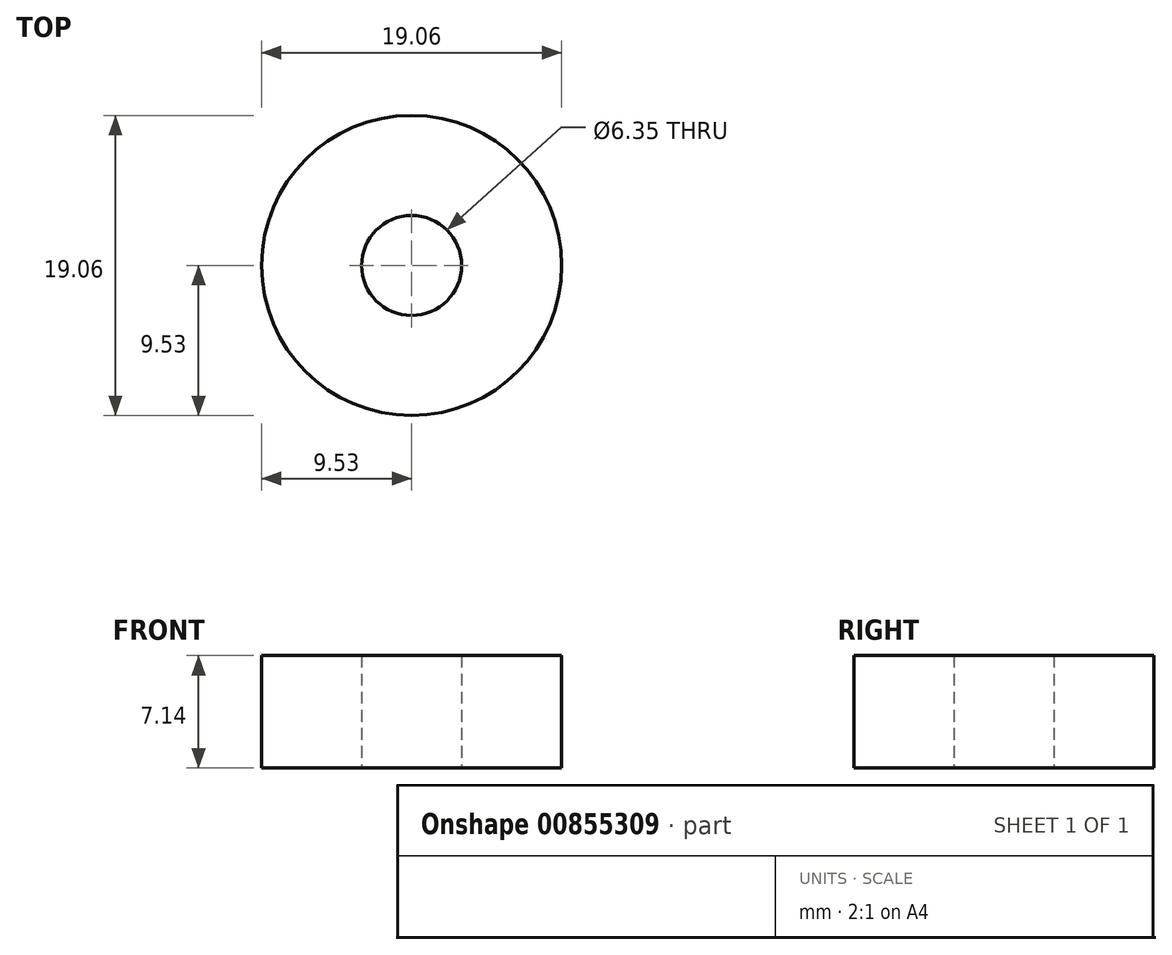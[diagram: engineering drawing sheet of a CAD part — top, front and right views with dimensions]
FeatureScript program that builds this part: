
annotation { "Feature Type Name" : "Feature", "Feature Type Description" : "" }
export const myFeature = defineFeature(function(context is Context, id is Id, definition is map)
    precondition{}
    {
        {
            var Q0;
            Q0=qCreatedBy(makeId("Top.planeOp"),FACE);
            var sketch = newSketch(context, id + "F0", { "sketchPlane" : qUnion([Q0])});
            skCircle(sketch, "E0", {"center": v(0, 0) * mm, "radius": 3.17 * mm});
            skCircle(sketch, "E1", {"center": v(0, 0) * mm, "radius": 9.53 * mm});
            skSolve(sketch);
        }
        {
            var Q0;
            Q0=makeQuery(id+"F0.imprint","IMPRINT",FACE,{"disambiguationData":[TD([[makeQuery(id+"F0.imprint","IMPRINT",EDGE,{"derivedFrom":sQuery(id+"F0.wireOp",EDGE,"E0")}),-1.0]])]});
            extrude(context, id + "F1", {"entities" : qUnion([Q0]), "depth" : 7.14 * mm, "offsetDistance" : 25 * mm});
        }
    });
